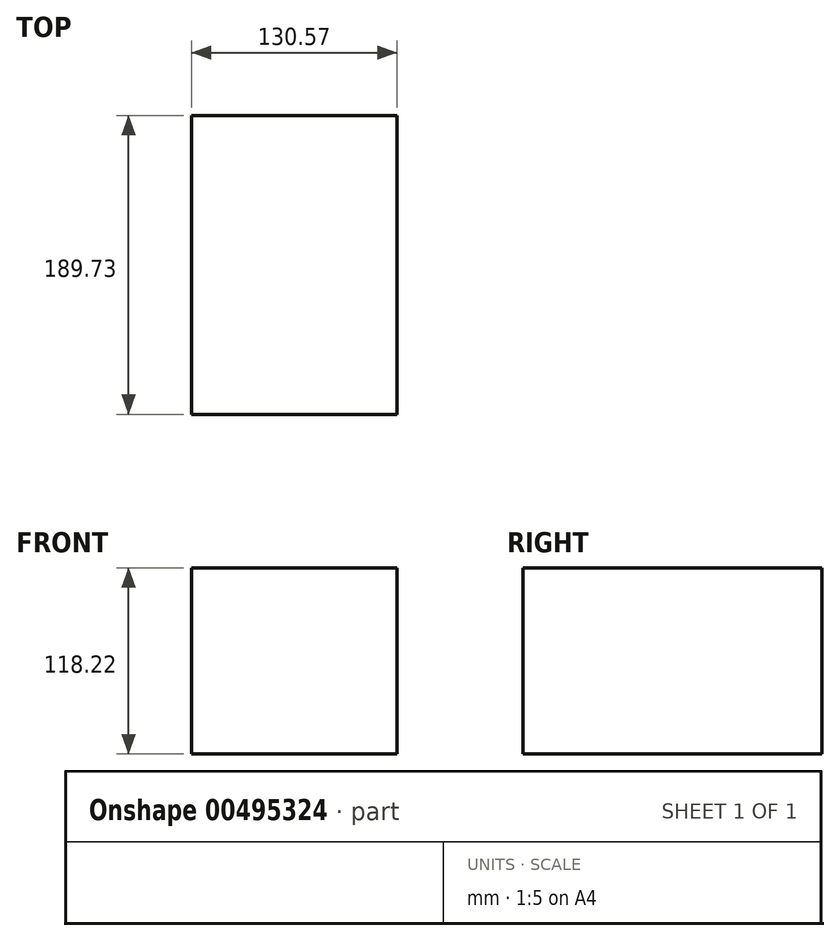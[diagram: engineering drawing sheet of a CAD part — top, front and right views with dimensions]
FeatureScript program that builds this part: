
annotation { "Feature Type Name" : "Feature", "Feature Type Description" : "" }
export const myFeature = defineFeature(function(context is Context, id is Id, definition is map)
    precondition{}
    {
        {
            var Q0;
            Q0=qCreatedBy(makeId("Front.planeOp"),FACE);
            var sketch = newSketch(context, id + "F0", { "sketchPlane" : qUnion([Q0])});
            skLineSegment(sketch, "E0.bottom", {"start": v(-57.15, 59.48) * mm, "end": v(73.42, 59.48) * mm});
            skLineSegment(sketch, "E0.top", {"start": v(-57.15, -58.74) * mm, "end": v(73.42, -58.74) * mm});
            skLineSegment(sketch, "E0.left", {"start": v(-57.15, 59.48) * mm, "end": v(-57.15, -58.74) * mm});
            skLineSegment(sketch, "E0.right", {"start": v(73.42, 59.48) * mm, "end": v(73.42, -58.74) * mm});
            skSolve(sketch);
        }
        {
            var Q0;
            Q0=makeQuery(id+"F0.imprint","IMPRINT",FACE,{"disambiguationData":[TD([[makeQuery(id+"F0.imprint","IMPRINT",EDGE,{"derivedFrom":sQuery(id+"F0.wireOp",EDGE,"E0.bottom")}),-1.0]])]});
            extrude(context, id + "F1", {"entities" : qUnion([Q0]), "depth" : 85.34 * mm, "hasSecondDirection" : true, "secondDirectionOppositeDirection" : true, "secondDirectionDepth" : 104.4 * mm});
        }
        {
            var Q0;
            Q0=makeQuery(id+"F1.opExtrude","SWEPT_FACE",FACE,{"disambiguationData":[OSD([sQuery(id+"F0.wireOp",EDGE,"E0.right")])]});
            var sketch = newSketch(context, id + "F2", { "sketchPlane" : qUnion([Q0])});
            skLineSegment(sketch, "E1.bottom", {"start": v(-33.94, 90.07) * mm, "end": v(44.94, 90.07) * mm});
            skLineSegment(sketch, "E1.top", {"start": v(-33.94, -108.77) * mm, "end": v(44.94, -108.77) * mm});
            skLineSegment(sketch, "E1.left", {"start": v(-33.94, 90.07) * mm, "end": v(-33.94, -108.77) * mm});
            skLineSegment(sketch, "E1.right", {"start": v(44.94, 90.07) * mm, "end": v(44.94, -108.77) * mm});
            skSolve(sketch);
        }
        {
            var Q0;
            Q0 = qSketchRegion(id + "F2", true);
            extrude(context, id + "F3", {"entities" : qUnion([Q0]), "operationType" : NewBodyOperationType.ADD, "endBound" : BoundingType.UP_TO_NEXT, "oppositeDirection" : true, "depth" : 25.4 * mm});
        }
    });
